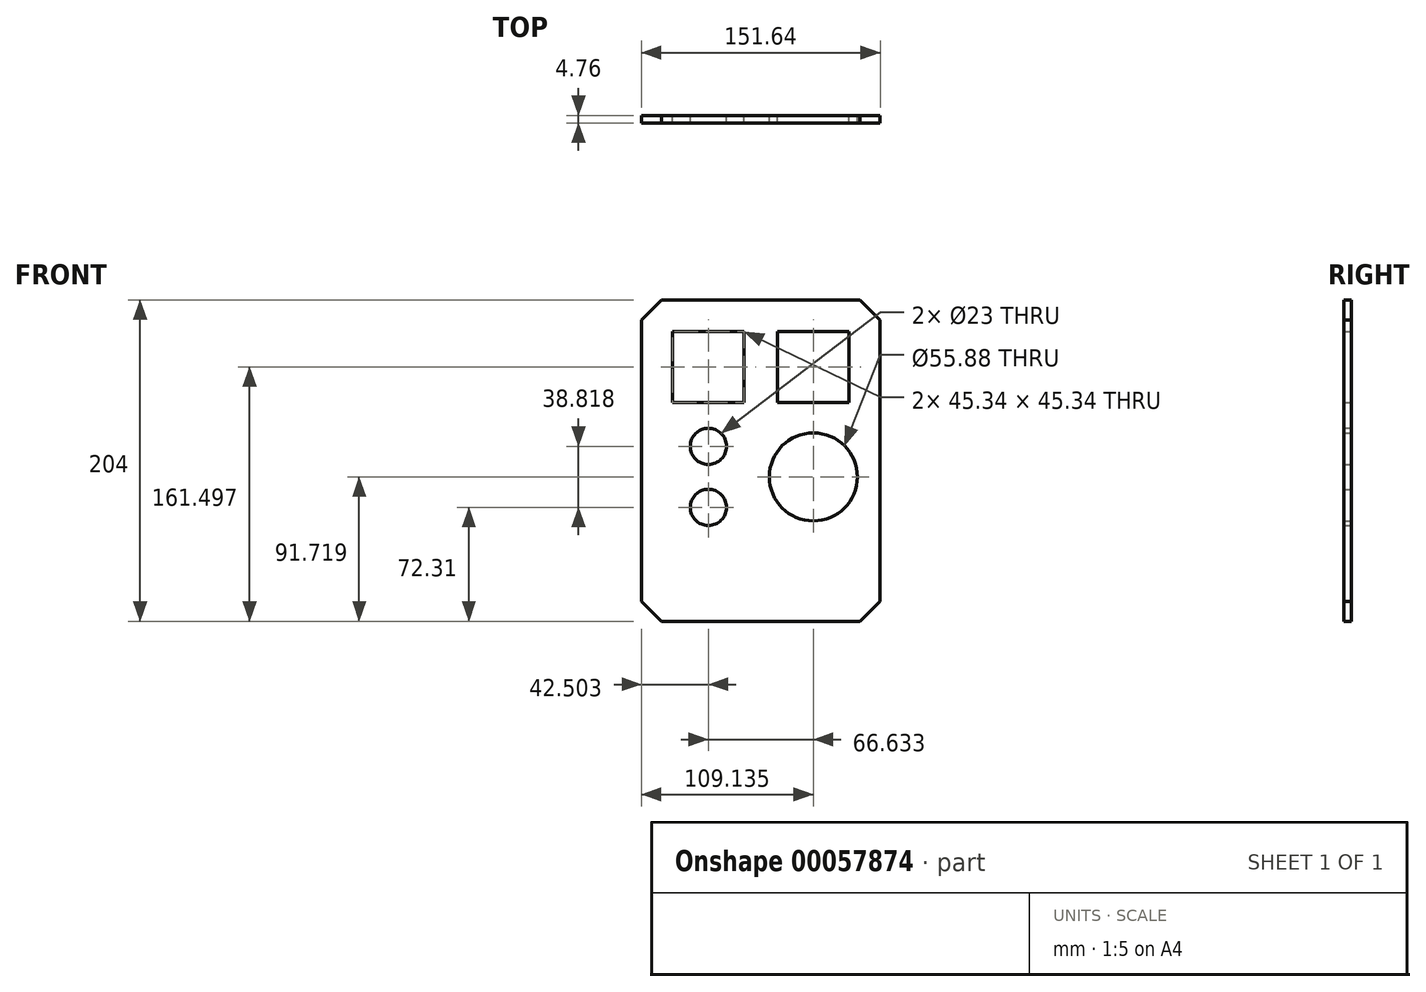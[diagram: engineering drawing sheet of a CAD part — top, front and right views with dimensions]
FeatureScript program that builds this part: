
annotation { "Feature Type Name" : "Feature", "Feature Type Description" : "" }
export const myFeature = defineFeature(function(context is Context, id is Id, definition is map)
    precondition{}
    {
        {
            var Q0;
            Q0=qCreatedBy(makeId("Front.planeOp"),FACE);
            var sketch = newSketch(context, id + "F0", { "sketchPlane" : qUnion([Q0])});
            skLineSegment(sketch, "E0.bottom", {"start": v(0, 0) * mm, "end": v(151.64, 0) * mm});
            skLineSegment(sketch, "E0.top", {"start": v(0, -204) * mm, "end": v(151.64, -204) * mm});
            skLineSegment(sketch, "E0.left", {"start": v(0, 0) * mm, "end": v(0, -204) * mm});
            skLineSegment(sketch, "E0.right", {"start": v(151.64, 0) * mm, "end": v(151.64, -204) * mm});
            skLineSegment(sketch, "E1.bottom", {"start": v(19.83, -19.83) * mm, "end": v(65.17, -19.83) * mm});
            skLineSegment(sketch, "E1.top", {"start": v(19.83, -65.17) * mm, "end": v(65.17, -65.17) * mm});
            skLineSegment(sketch, "E1.left", {"start": v(19.83, -19.83) * mm, "end": v(19.83, -65.17) * mm});
            skLineSegment(sketch, "E1.right", {"start": v(65.17, -19.83) * mm, "end": v(65.17, -65.17) * mm});
            skLineSegment(sketch, "E2.bottom", {"start": v(86.47, -19.83) * mm, "end": v(131.8, -19.83) * mm});
            skLineSegment(sketch, "E2.top", {"start": v(86.47, -65.17) * mm, "end": v(131.8, -65.17) * mm});
            skLineSegment(sketch, "E2.left", {"start": v(86.47, -19.83) * mm, "end": v(86.47, -65.17) * mm});
            skLineSegment(sketch, "E2.right", {"start": v(131.8, -19.83) * mm, "end": v(131.8, -65.17) * mm});
            skLineSegment(sketch, "E3.0", {"start": v(18.37, -18.37) * mm, "end": v(66.63, -18.37) * mm, "construction": true});
            skLineSegment(sketch, "E3.1", {"start": v(18.37, -18.37) * mm, "end": v(18.37, -66.63) * mm, "construction": true});
            skLineSegment(sketch, "E3.2", {"start": v(18.37, -66.63) * mm, "end": v(66.63, -66.63) * mm, "construction": true});
            skLineSegment(sketch, "E3.3", {"start": v(66.63, -18.37) * mm, "end": v(66.63, -66.63) * mm, "construction": true});
            skLineSegment(sketch, "E4.bottom", {"start": v(85, -18.37) * mm, "end": v(133.27, -18.37) * mm, "construction": true});
            skLineSegment(sketch, "E4.top", {"start": v(85, -66.63) * mm, "end": v(133.27, -66.63) * mm, "construction": true});
            skLineSegment(sketch, "E4.left", {"start": v(85, -18.37) * mm, "end": v(85, -66.63) * mm, "construction": true});
            skLineSegment(sketch, "E4.right", {"start": v(133.27, -18.37) * mm, "end": v(133.27, -66.63) * mm, "construction": true});
            skLineSegment(sketch, "E5", {"start": v(86.47, -65.17) * mm, "end": v(85, -66.63) * mm});
            skLineSegment(sketch, "E6", {"start": v(0, -66.63) * mm, "end": v(18.37, -66.63) * mm, "construction": true});
            skLineSegment(sketch, "E7", {"start": v(66.63, -66.63) * mm, "end": v(85, -66.63) * mm, "construction": true});
            skLineSegment(sketch, "E8", {"start": v(133.27, -66.63) * mm, "end": v(151.64, -66.63) * mm, "construction": true});
            skLineSegment(sketch, "E9", {"start": v(85, -18.37) * mm, "end": v(85, 0) * mm, "construction": true});
            skCircle(sketch, "E10", {"center": v(42.5, -92.87) * mm, "radius": 11.5 * mm});
            skCircle(sketch, "E11", {"center": v(42.5, -92.87) * mm, "radius": 14.5 * mm, "construction": true});
            skCircle(sketch, "E12", {"center": v(42.5, -131.69) * mm, "radius": 11.5 * mm});
            skCircle(sketch, "E13", {"center": v(42.5, -131.69) * mm, "radius": 14.5 * mm, "construction": true});
            skLineSegment(sketch, "E14", {"start": v(42.5, -65.17) * mm, "end": v(42.5, -92.87) * mm, "construction": true});
            skCircle(sketch, "E15", {"center": v(109.14, -112.28) * mm, "radius": 33.9 * mm, "construction": true});
            skLineSegment(sketch, "E16", {"start": v(109.14, -65.17) * mm, "end": v(109.14, -112.28) * mm, "construction": true});
            skCircle(sketch, "E17", {"center": v(109.14, -112.28) * mm, "radius": 27.94 * mm});
            skLineSegment(sketch, "E18", {"start": v(109.14, -78.37) * mm, "end": v(42.5, -78.37) * mm});
            skLineSegment(sketch, "E19", {"start": v(42.5, -146.19) * mm, "end": v(109.14, -146.19) * mm});
            skSolve(sketch);
        }
        {
            var Q0;
            Q0=makeQuery(id+"F0.imprint","IMPRINT",FACE,{"disambiguationData":[TD([[makeQuery(id+"F0.imprint","IMPRINT",EDGE,{"derivedFrom":sQuery(id+"F0.wireOp",EDGE,"E0.bottom")}),-1.0]])]});
            extrude(context, id + "F1", {"entities" : qUnion([Q0]), "depth" : 4.76 * mm});
        }
        {
            var Q0;
            Q0=makeQuery(id+"F1.opExtrude","SWEPT_EDGE",EDGE,{"disambiguationData":[OSD([sQuery(id+"F0.wireOp",EDGE,"E0.bottom"),sQuery(id+"F0.wireOp",EDGE,"E0.right")])]});
            var Q1;
            Q1=makeQuery(id+"F1.opExtrude","SWEPT_EDGE",EDGE,{"disambiguationData":[OSD([sQuery(id+"F0.wireOp",EDGE,"E0.bottom"),sQuery(id+"F0.wireOp",EDGE,"E0.left")])]});
            var Q2;
            Q2=makeQuery(id+"F1.opExtrude","SWEPT_EDGE",EDGE,{"disambiguationData":[OSD([sQuery(id+"F0.wireOp",EDGE,"E0.top"),sQuery(id+"F0.wireOp",EDGE,"E0.left")])]});
            var Q3;
            Q3=makeQuery(id+"F1.opExtrude","SWEPT_EDGE",EDGE,{"disambiguationData":[OSD([sQuery(id+"F0.wireOp",EDGE,"E0.top"),sQuery(id+"F0.wireOp",EDGE,"E0.right")])]});
            chamfer(context, id + "F2", {"entities" : qUnion([Q0, Q1, Q2, Q3]), "width" : 12.7 * mm, "tangentPropagation" : true});
        }
    });
